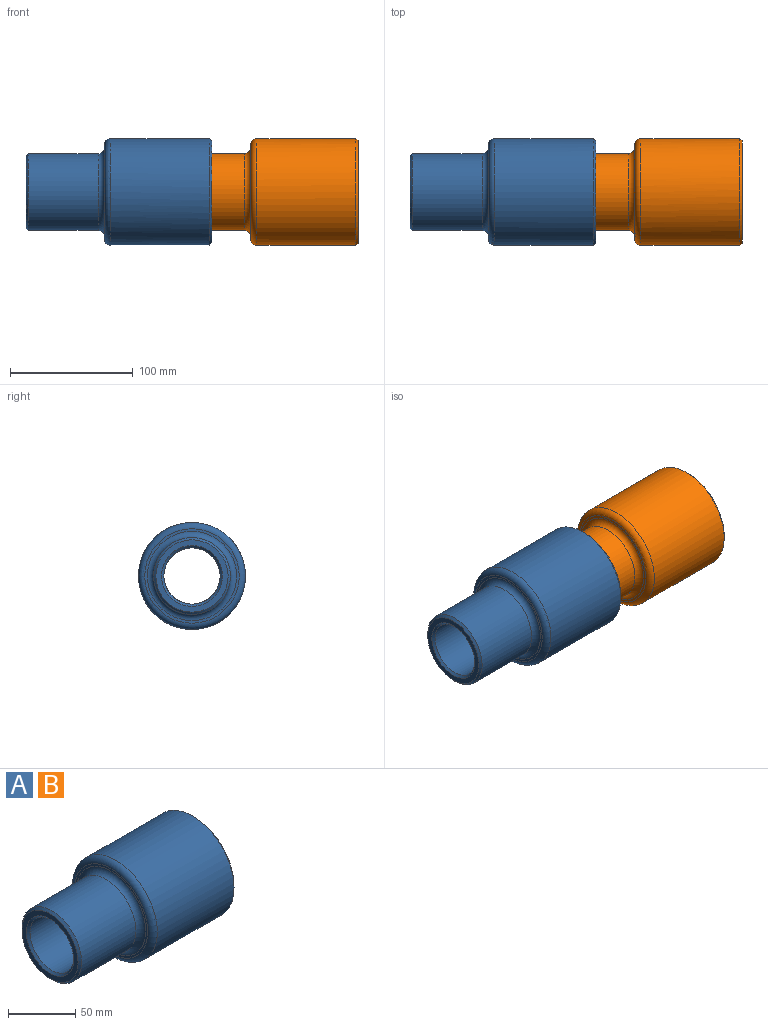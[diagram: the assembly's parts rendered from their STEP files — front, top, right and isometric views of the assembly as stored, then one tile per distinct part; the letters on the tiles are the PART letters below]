
ASSEMBLY  parts=2 mates=2
PART A: 37 faces, bbox 151.6x94.4x94.4 mm
  f0: plane 83.37x83.37mm, normal (1,0,0), area 1900.2mm2, adj f10,f11,f28,f30,f32,f34,f36
  f1: plane 58.9x58.9mm, normal (-1,0,0), area 785mm2, adj f8,f9
  f2: cylinder r=22.94mm len=102.81mm, axis (-1,0,0), area 14819.7mm2, adj f9,f14
  f3: plane 57.63x57.63mm, normal (1,0,0), area 568.4mm2, adj f14,f15
  f4: cylinder r=31.35mm len=62.71mm, axis (-1,0,0), area 7531.4mm2, adj f10,f15,f27,f29,f31,f33,f35
  f5: cylinder r=43.59mm len=87.18mm, axis (-1,0,0), area 22068.5mm2, adj f11,f12
  f6: plane 77.02x77.02mm, normal (-1,0,0), area 488.7mm2, adj f12,f13
  f7: cylinder r=31.35mm len=62.71mm, axis (-1,0,0), area 11241.2mm2, adj f8,f13
  f8: cone r=29.45mm half-angle=45deg, axis (1,0,0), area 514.6mm2, adj f1,f7
  f9: cone r=22.94mm half-angle=45deg, axis (-1,0,0), area 404.5mm2, adj f1,f2
  f10: cone r=33.26mm half-angle=45deg, axis (1,0,0), area 514.5mm2, adj f0,f4,f27,f28,f35,f36
  f11: cone r=43.59mm half-angle=45deg, axis (-1,0,0), area 721.7mm2, adj f0,f5
  f12: torus R=38.51mm, axis (1,0,0), area 2092.9mm2, adj f5,f6
  f13: torus R=36.43mm, axis (1,0,0), area 1664.6mm2, adj f6,f7
  f14: cone r=25.48mm half-angle=45deg, axis (1,0,0), area 546.5mm2, adj f2,f3
  f15: cone r=31.35mm half-angle=45deg, axis (1,0,0), area 679mm2, adj f3,f4
  f16: plane 8.83x4.51mm, normal (1,0,0), area 37.2mm2, adj f21,f23,f24,f31
  f17: cylinder r=38.1mm len=22.86mm, axis (1,0,0), area 209.3mm2, adj f20,f23,f26,f32
  f18: plane 22.86x4.69mm, normal (0,1,0), area 107.2mm2, adj f24,f26,f27,f28
  f19: plane 22.86x4.69mm, normal (0,-1,0), area 107.2mm2, adj f20,f21,f35,f36
  f20: cylinder r=1.27mm len=22.86mm, axis (1,0,0), area 42.1mm2, adj f17,f19,f22,f34
  f21: cylinder r=1.27mm len=4.69mm, axis (0,0,1), area 9mm2, adj f16,f19,f22,f33
  f22: sphere r=1.27mm, area 2.3mm2, adj f20,f21,f23
  f23: torus R=36.83mm, axis (1,0,0), area 18mm2, adj f16,f17,f22,f25
  f24: cylinder r=1.27mm len=4.69mm, axis (0,0,-1), area 9mm2, adj f16,f18,f25,f29
  f25: sphere r=1.27mm, area 2.3mm2, adj f23,f24,f26
  f26: cylinder r=1.27mm len=22.86mm, axis (1,0,0), area 42.1mm2, adj f17,f18,f25,f30
  f27: cylinder r=1.27mm len=23.06mm, axis (-1,0,0), area 38.9mm2, adj f4,f10,f18,f28,f29
  f28: cylinder r=1.27mm len=4.89mm, axis (0,0,-1), area 8.6mm2, adj f0,f10,f18,f27,f30
  f29: bspline ~3.1x2.99mm, area 5.1mm2, adj f4,f24,f27,f31
  f30: torus R=2.54mm, axis (-1,0,0), area 5mm2, adj f0,f26,f28,f32
  f31: torus R=32.62mm, axis (1,0,0), area 17.2mm2, adj f4,f16,f29,f33
  f32: torus R=39.37mm, axis (-1,0,0), area 18.5mm2, adj f0,f17,f30,f34
  f33: bspline ~3.1x2.99mm, area 5.1mm2, adj f4,f21,f31,f35
  f34: torus R=2.54mm, axis (-1,0,0), area 5mm2, adj f0,f20,f32,f36
  f35: cylinder r=1.27mm len=23.06mm, axis (-1,0,0), area 38.9mm2, adj f4,f10,f19,f33,f36
  f36: cylinder r=1.27mm len=4.89mm, axis (0,0,1), area 8.6mm2, adj f0,f10,f19,f34,f35
PART B: same geometry as A
PLACE A t=(-50.94,10.05,113.51)mm
PLACE B rot(axis=(1,0,0),125deg) t=(68.33,10.05,113.51)mm
MATE revolute B.f2 <-> A.f2  axis (-1,0,0) through (15.89,10.05,113.51)mm
MATE parallel B.f2 <-> A.f0  axis (-1,0,0) through (49.5,10.05,113.51)mm
